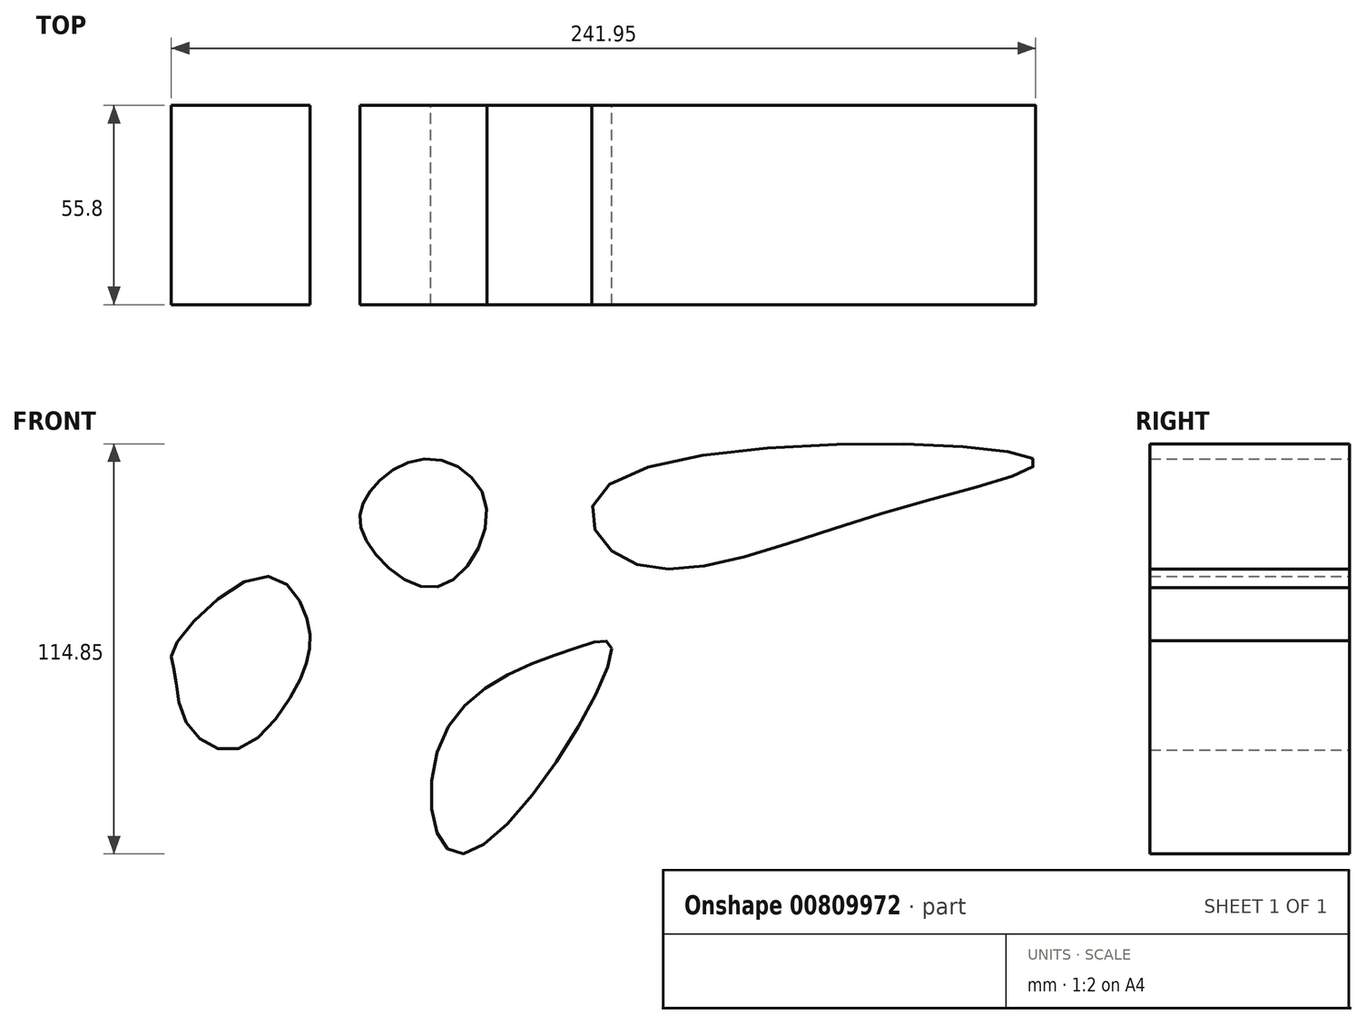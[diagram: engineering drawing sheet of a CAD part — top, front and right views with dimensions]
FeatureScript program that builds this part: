
annotation { "Feature Type Name" : "Feature", "Feature Type Description" : "" }
export const myFeature = defineFeature(function(context is Context, id is Id, definition is map)
    precondition{}
    {
        {
            var Q0;
            Q0=qCreatedBy(makeId("Front.planeOp"),FACE);
            var sketch = newSketch(context, id + "F0", { "sketchPlane" : qUnion([Q0])});
            skFitSpline(sketch, "E0", {"points": [v(-50.4, -20.7) * mm, v(-53.84, -5.7) * mm, v(-54, 0) * mm, v(-28.7, 20.23) * mm, v(-17.1, 9.9) * mm, v(-15.9, 0) * mm, v(-19.65, -10.95) * mm, v(-36.2, -28.18) * mm, v(-50.4, -20.7) * mm]});
            skFitSpline(sketch, "E1", {"points": [v(0, 30.3) * mm, v(0, 42.44) * mm, v(16.65, 53.1) * mm, v(33.54, 40.28) * mm, v(19.8, 17.26) * mm, v(0, 30.3) * mm]});
            skFitSpline(sketch, "E2", {"points": [v(68.65, 0) * mm, v(26.98, -57.49) * mm, v(21.3, -25.08) * mm, v(58.13, 0) * mm, v(68.65, 0) * mm]});
            skFitSpline(sketch, "E3", {"points": [v(186.51, 53.21) * mm, v(66.76, 45) * mm, v(73.07, 24.6) * mm, v(144.42, 37.85) * mm, v(186.51, 53.21) * mm]});
            skSolve(sketch);
        }
        {
            var Q0;
            Q0 = qSketchRegion(id + "F0", true);
            extrude(context, id + "F1", {"entities" : qUnion([Q0]), "depth" : 55.8 * mm, "offsetDistance" : 25.4 * mm});
        }
    });
